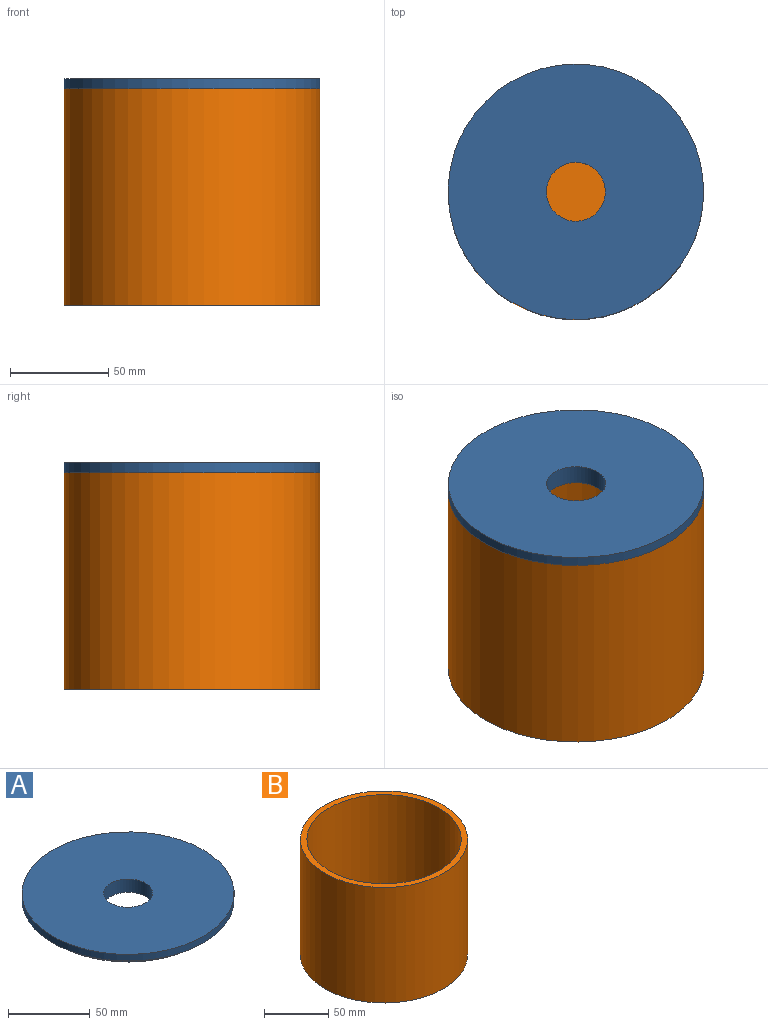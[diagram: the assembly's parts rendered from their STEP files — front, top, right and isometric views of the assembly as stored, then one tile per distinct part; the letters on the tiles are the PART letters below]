
ASSEMBLY  parts=2 mates=1
PART A: 6 faces, bbox 130x130x10 mm
  f0: cylinder r=15mm len=30mm, axis (0,0,1), area 942.5mm2, adj f2,f3
  f1: cylinder r=59mm len=118mm, axis (0,0,1), area 1853.5mm2, adj f2,f5
  f2: plane 118x118mm, normal (0,0,-1), area 10229mm2, adj f0,f1
  f3: plane 130x130mm, normal (0,0,1), area 12566.4mm2, adj f0,f4
  f4: cylinder r=65mm len=130mm, axis (0,0,1), area 2042mm2, adj f3,f5
  f5: plane 130x130mm, normal (0,0,-1), area 2337.3mm2, adj f1,f4
PART B: 5 faces, bbox 130x130x110 mm
  f0: plane 120x120mm, normal (0,0,1), area 11309.7mm2, adj f1
  f1: cylinder r=60mm len=120mm, axis (0,0,-1), area 39584.1mm2, adj f0,f3
  f2: cylinder r=65mm len=130mm, axis (0,0,-1), area 44924.8mm2, adj f3,f4
  f3: plane 130x130mm, normal (0,0,1), area 1963.5mm2, adj f1,f2
  f4: plane 130x130mm, normal (0,0,-1), area 13273.2mm2, adj f2
PLACE A rot(axis=(0.08,1,0.02),0deg) t=(139.81,-12.88,100)mm
PLACE B rot(axis=(0,1,0),0deg) t=(0,0,5)mm
MATE fastened B.f1 <-> A.f0  axis (0,0,-1) through (0,0,115)mm
